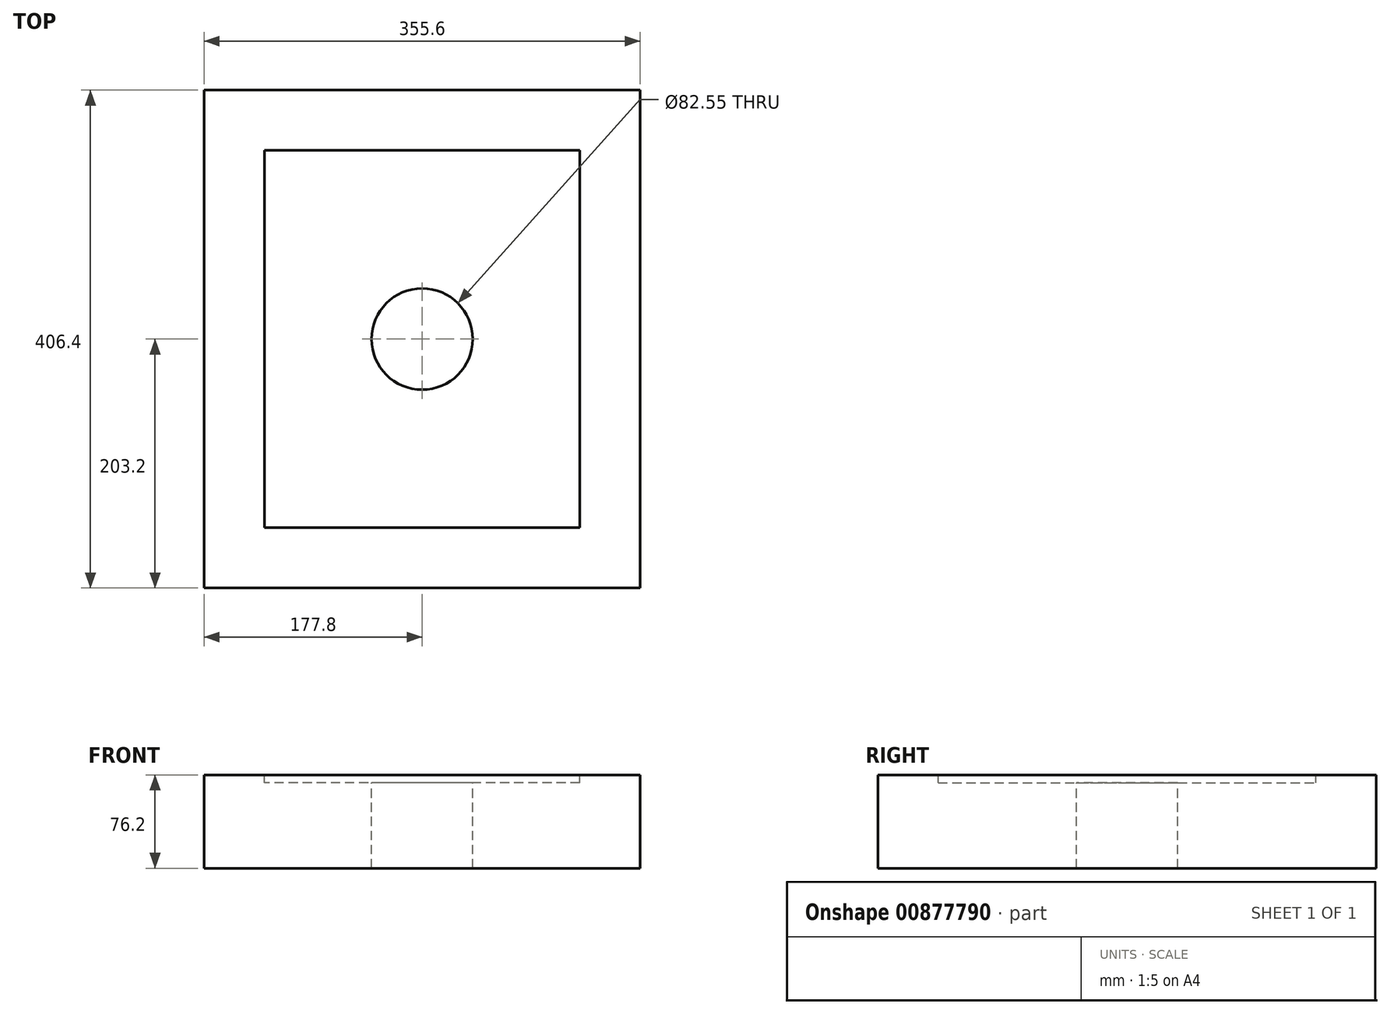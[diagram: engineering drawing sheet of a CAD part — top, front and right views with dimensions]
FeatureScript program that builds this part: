
annotation { "Feature Type Name" : "Feature", "Feature Type Description" : "" }
export const myFeature = defineFeature(function(context is Context, id is Id, definition is map)
    precondition{}
    {
        {
            var Q0;
            Q0=qCreatedBy(makeId("Top.planeOp"),FACE);
            var sketch = newSketch(context, id + "F0", { "sketchPlane" : qUnion([Q0])});
            skLineSegment(sketch, "E0.bottom", {"start": v(177.8, -203.2) * mm, "end": v(-177.8, -203.2) * mm});
            skLineSegment(sketch, "E0.top", {"start": v(177.8, 203.2) * mm, "end": v(-177.8, 203.2) * mm});
            skLineSegment(sketch, "E0.left", {"start": v(177.8, -203.2) * mm, "end": v(177.8, 203.2) * mm});
            skLineSegment(sketch, "E0.right", {"start": v(-177.8, -203.2) * mm, "end": v(-177.8, 203.2) * mm});
            skPoint(sketch, "E0.middle", {"position": v(0, 0) * mm});
            skSolve(sketch);
        }
        {
            var Q0;
            Q0=makeQuery(id+"F0.imprint","IMPRINT",FACE,{"disambiguationData":[TD([[makeQuery(id+"F0.imprint","IMPRINT",EDGE,{"derivedFrom":sQuery(id+"F0.wireOp",EDGE,"E0.bottom")}),-1.0]])]});
            extrude(context, id + "F1", {"entities" : qUnion([Q0]), "depth" : 76.2 * mm, "offsetDistance" : 25.4 * mm});
        }
        {
            var Q0;
            Q0=makeQuery(id+"F1.opExtrude","CAP_FACE",FACE,{"disambiguationData":[OSD([sQuery(id+"F0.wireOp",EDGE,"E0.bottom"),sQuery(id+"F0.wireOp",EDGE,"E0.top"),sQuery(id+"F0.wireOp",EDGE,"E0.left"),sQuery(id+"F0.wireOp",EDGE,"E0.right")])],"isStart":false});
            var sketch = newSketch(context, id + "F2", { "sketchPlane" : qUnion([Q0])});
            skCircle(sketch, "E1", {"center": v(0, 0) * mm, "radius": 41.27 * mm});
            skSolve(sketch);
        }
        {
            var Q0;
            Q0=makeQuery(id+"F2.imprint","IMPRINT",FACE,{"disambiguationData":[TD([[makeQuery(id+"F2.imprint","IMPRINT",EDGE,{"derivedFrom":sQuery(id+"F2.wireOp",EDGE,"E1")}),1.0]])]});
            extrude(context, id + "F3", {"entities" : qUnion([Q0]), "operationType" : NewBodyOperationType.REMOVE, "endBound" : BoundingType.THROUGH_ALL, "oppositeDirection" : true, "depth" : 25.4 * mm, "offsetDistance" : 25.4 * mm});
        }
        {
            var Q0;
            Q0=makeQuery(id+"F1.opExtrude","CAP_FACE",FACE,{"disambiguationData":[OSD([sQuery(id+"F0.wireOp",EDGE,"E0.bottom"),sQuery(id+"F0.wireOp",EDGE,"E0.top"),sQuery(id+"F0.wireOp",EDGE,"E0.left"),sQuery(id+"F0.wireOp",EDGE,"E0.right")])],"isStart":false});
            var sketch = newSketch(context, id + "F4", { "sketchPlane" : qUnion([Q0])});
            skLineSegment(sketch, "E2.bottom", {"start": v(128.59, -153.99) * mm, "end": v(-128.59, -153.99) * mm});
            skLineSegment(sketch, "E2.top", {"start": v(128.59, 153.99) * mm, "end": v(-128.59, 153.99) * mm});
            skLineSegment(sketch, "E2.left", {"start": v(128.59, -153.99) * mm, "end": v(128.59, 153.99) * mm});
            skLineSegment(sketch, "E2.right", {"start": v(-128.59, -153.99) * mm, "end": v(-128.59, 153.99) * mm});
            skPoint(sketch, "E2.middle", {"position": v(0, 0) * mm});
            skSolve(sketch);
        }
        {
            var Q0;
            Q0=makeQuery(id+"F4.imprint","IMPRINT",FACE,{"disambiguationData":[TD([[makeQuery(id+"F4.imprint","IMPRINT",EDGE,{"derivedFrom":sQuery(id+"F4.wireOp",EDGE,"E2.bottom")}),-1.0]])]});
            extrude(context, id + "F5", {"entities" : qUnion([Q0]), "operationType" : NewBodyOperationType.REMOVE, "oppositeDirection" : true, "depth" : 6.35 * mm, "offsetDistance" : 25.4 * mm});
        }
    });
